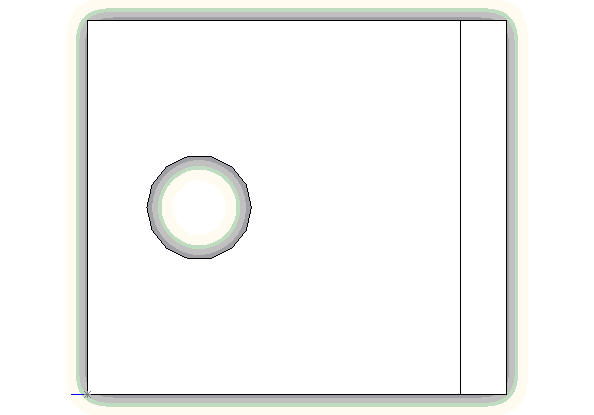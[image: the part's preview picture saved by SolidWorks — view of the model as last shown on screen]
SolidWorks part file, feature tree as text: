
SOLIDWORKS PART (.sldprt)
format: sldprt  version: not decoded by parser v0  size: 108,544 bytes
history: native  units: mm
features: sketch x3, cut_extrude x2, material x1, extrude x1 (+13 scaffold rows collapsed)
feature tree (20):
  scaffold x13  (default folders/planes/origin — collapsed)
  material  "Material <not specified>"
  sketch  "Sketch1"  dims[D1=1.5748mm D2=1.5748mm D3=14.2748mm D4=14.2748mm]
  extrude  "Extrude1"  Depth=12.7mm
  sketch  "Sketch2"  dims[D1=3.556mm D2=6.35mm D3=10.4648mm]
  cut_extrude  "Cut-Extrude1"  Depth=7.1374mm
  sketch  "Sketch4"  dims[D1=3.556mm D2=10.4648mm]
  cut_extrude  "Cut-Extrude2"  Depth=7.1374mm
decode coverage: 6 of 6 modeling features carry decoded parameters
note: suppression state not decoded; provenance and decode notes live in map.json
